# Revit family: Gira_282026
name_source: partatom
category: Electrical Fixtures
revit_build: Autodesk Revit 2017 (Build: 20160225_1515(x64)
units: mm (PartAtom-declared; Revit-internal decimal feet)

## family parameters
Cut with Voids When Loaded = No
Host = Face
Maintain Annotation Orientation = Yes
Part Type = Normal
Room Calculation Point = No
Round Connector Dimension = Use Diameter
Shared = No

## types (1)
- Rasiersteckd. 115 - 230 V System 55 F Alu
    Available = Yes
    Category = Rasiersteckdose
    Data sheet (1) = https://katalog.gira.de
    Default Elevation = 1219 mm
    Farbe = aluminium
    GTIN = 4010337016793
    HAN = 282026
    Halogenfrei = No
    HeinzeBIM = https://bimportal.heinze.de
    Keynote = Sys55_Rasiersteckdose_115-230V
    Manufacturer URL = https://www.gira.de
    Mit Klappdeckel = No
    Montageart = unter Putz
    Name = Rasiersteckd. 115 - 230 V System 55 F Alu
    Nennspannung hoher Wert = 230 Volt
    Nennspannung niedriger Wert = 115 Volt
    Oberfläche = sonstige
    Region = DE
    Spannung umschaltbar = Yes
    Transparent = No
    URL = http://katalog.gira.de
    Werkstoff = sonstige
    Werkstoffgüte = sonstige
    Zusammenstellung = Basiselement mit Adapterplatte

## geometry (parser evidence)
native form markers: Blend x2, Sweep x3
no freeform markers — native parametric forms only
